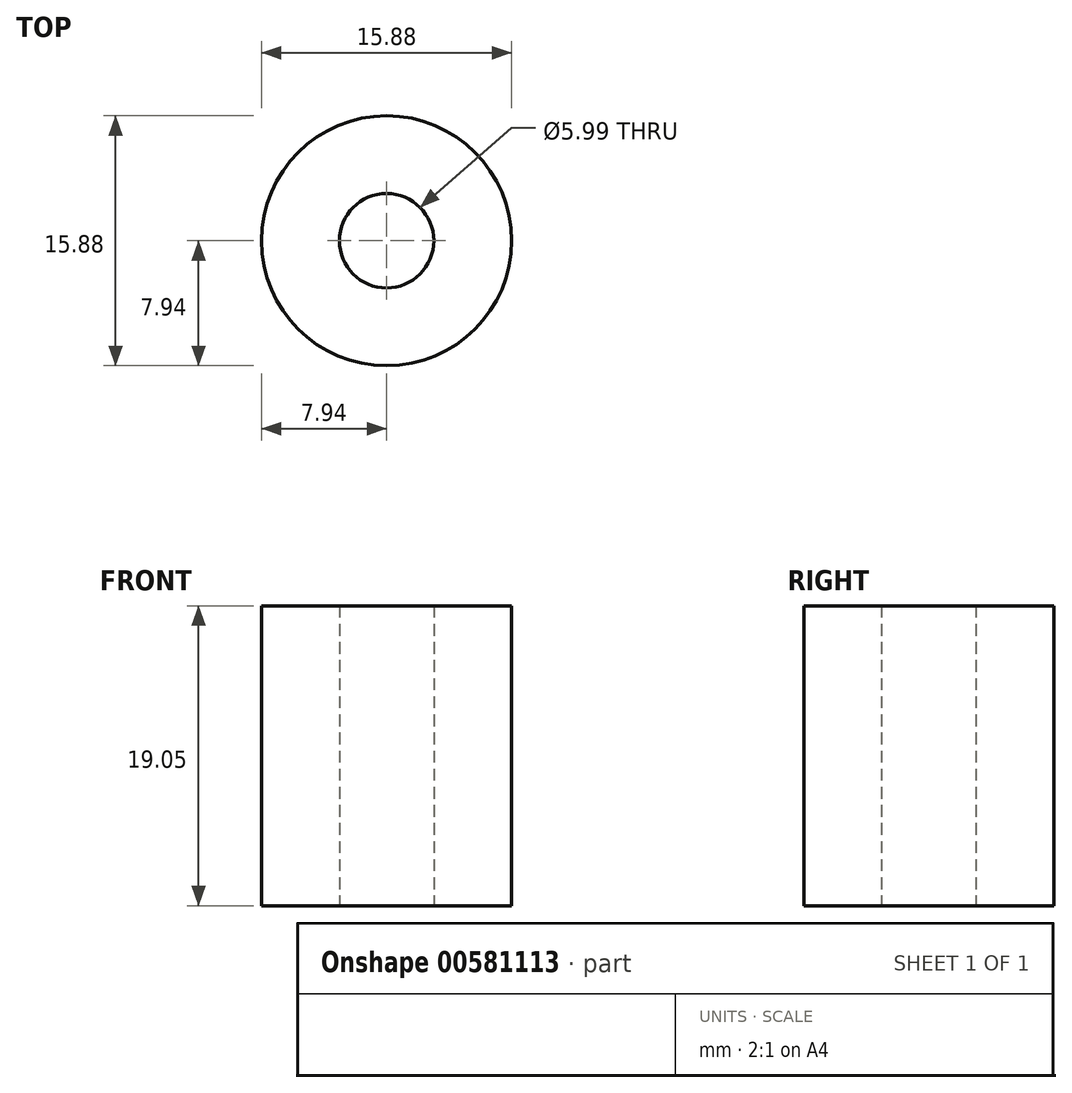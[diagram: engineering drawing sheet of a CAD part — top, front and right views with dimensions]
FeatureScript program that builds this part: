
annotation { "Feature Type Name" : "Feature", "Feature Type Description" : "" }
export const myFeature = defineFeature(function(context is Context, id is Id, definition is map)
    precondition{}
    {
        {
            var Q0;
            Q0=qCreatedBy(makeId("Top.planeOp"),FACE);
            var sketch = newSketch(context, id + "F0", { "sketchPlane" : qUnion([Q0])});
            skCircle(sketch, "E0", {"center": v(0, 0) * mm, "radius": 3 * mm});
            skCircle(sketch, "E1", {"center": v(0, 0) * mm, "radius": 7.94 * mm});
            skSolve(sketch);
        }
        {
            var Q0;
            Q0=makeQuery(id+"F0.imprint","IMPRINT",FACE,{"disambiguationData":[TD([[makeQuery(id+"F0.imprint","IMPRINT",EDGE,{"derivedFrom":sQuery(id+"F0.wireOp",EDGE,"E0")}),-1.0]])]});
            extrude(context, id + "F1", {"entities" : qUnion([Q0]), "depth" : 19.05 * mm, "offsetDistance" : 25.4 * mm});
        }
    });
